# Revit family: LCAL22
name_source: partatom
category: Luminarias
units: mm (PartAtom-declared; Revit-internal decimal feet)

## family parameters
Compartido = Sí
Corte con vacíos al cargar = No
Cota de conector redondo = Diámetro de uso
Origen de luz = No
Punto de cálculo de habitación = No
Se basa en plano de trabajo = Sí
Siempre vertical = No
Tipo de pieza = Normal

## types (1)
- PERFIL_LCAL22
    Clips de Sujecion 22.2 = 4
    Descripción = PERFIL DE ALUMINIO TIPO ESQUINA CON DIFUSOR LECHOSO PARA ALOJAR TIRA LUMINOSA DE HASTA 12.2MM DE ANCHO. INSTALACION PARA ESQUINAS, PERFIL DE CLIP MONTADO IDEAL PARA ATENUAR EL BRILLO E INCORPORAR LA LUZ AL AMBIENTE.PRESENTACION DE 1.2 METROS. REQUEIRE ACCESORIOS COMO TAPA FINAL PARA EXTREMOS Y CLIPS DE SUJECION (CONSIDERAR 4 PZAS POR 1.20M)
    Elevación por defecto = 1219 mm
    Fabricante = BRILLANT
    Longitud = 1200 mm
    Modelo = LCAL22
    Tapa Final 22.1 = 1

## geometry (parser evidence)
native form markers: Blend x2
no freeform markers — native parametric forms only
